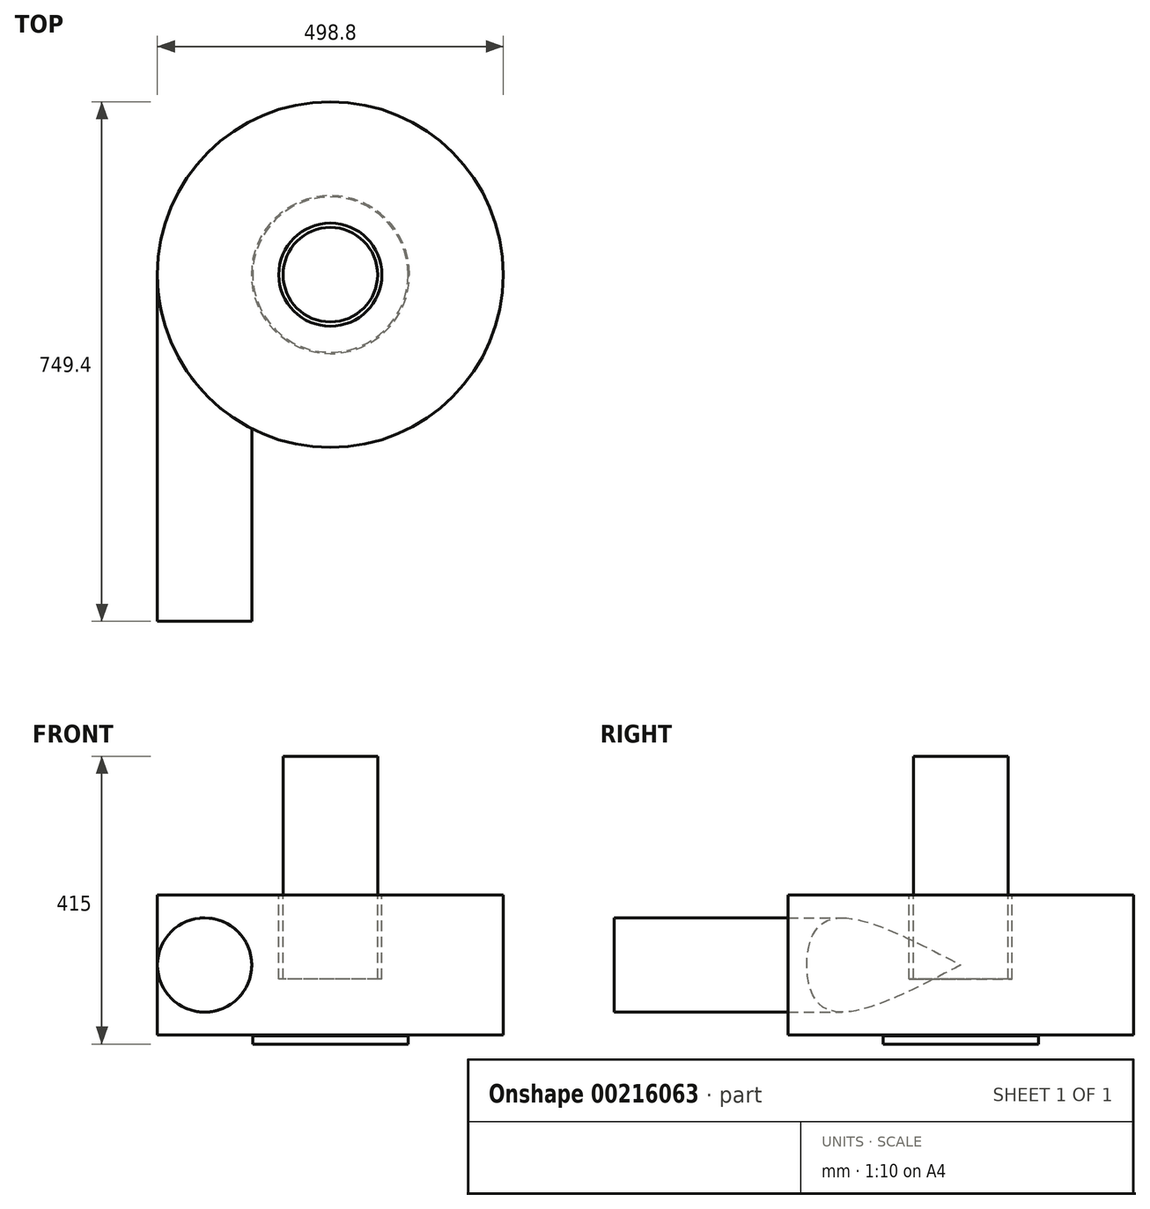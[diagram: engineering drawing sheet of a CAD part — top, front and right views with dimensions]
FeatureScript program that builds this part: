
annotation { "Feature Type Name" : "Feature", "Feature Type Description" : "" }
export const myFeature = defineFeature(function(context is Context, id is Id, definition is map)
    precondition{}
    {
        {
            var Q0;
            Q0=qCreatedBy(makeId("Front.planeOp"),FACE);
            var sketch = newSketch(context, id + "F0", { "sketchPlane" : qUnion([Q0])});
            skLineSegment(sketch, "E0", {"start": v(-114, 169) * mm, "end": v(-249.4, 169) * mm});
            skLineSegment(sketch, "E1", {"start": v(-249.4, 169) * mm, "end": v(-249.4, 371) * mm});
            skLineSegment(sketch, "E2", {"start": v(-249.4, 371) * mm, "end": v(-74.4, 371) * mm});
            skLineSegment(sketch, "E3", {"start": v(-74.4, 371) * mm, "end": v(-74.4, 250) * mm});
            skLineSegment(sketch, "E4", {"start": v(-74.4, 250) * mm, "end": v(-68.2, 250) * mm});
            skLineSegment(sketch, "E5", {"start": v(-68.2, 250) * mm, "end": v(-68.2, 371) * mm});
            skLineSegment(sketch, "E6", {"start": v(-68.2, 371) * mm, "end": v(0, 371) * mm});
            skLineSegment(sketch, "E7", {"start": v(-114, 169) * mm, "end": v(-112, 168) * mm});
            skLineSegment(sketch, "E8", {"start": v(-112, 168) * mm, "end": v(-112, 156) * mm});
            skLineSegment(sketch, "E9", {"start": v(-112, 156) * mm, "end": v(0, 156) * mm});
            skLineSegment(sketch, "E10", {"start": v(0, 371) * mm, "end": v(0, 156) * mm});
            skSolve(sketch);
        }
        {
            var Q0;
            Q0=makeQuery(id+"F0.imprint","IMPRINT",FACE,{"disambiguationData":[TD([[makeQuery(id+"F0.imprint","IMPRINT",EDGE,{"derivedFrom":sQuery(id+"F0.wireOp",EDGE,"E0")}),-1.0]])]});
            var Q1;
            Q1=sQuery(id+"F0.wireOp",EDGE,"E10");
            revolve(context, id + "F1", {"entities" : qUnion([Q0]), "axis" : qUnion([Q1]), "revolveType" : RevolveType.FULL});
        }
        {
            var Q0;
            Q0=qCreatedBy(makeId("Front.planeOp"),FACE);
            var sketch = newSketch(context, id + "F2", { "sketchPlane" : qUnion([Q0])});
            skCircle(sketch, "E11", {"center": v(-181.4, 270) * mm, "radius": 68 * mm});
            skSolve(sketch);
        }
        {
            var Q0;
            Q0=qSketchRegion(id+"F2",true);
            extrude(context, id + "F3", {"entities" : qUnion([Q0]), "operationType" : NewBodyOperationType.ADD, "depth" : 500 * mm});
        }
        {
            var Q0;
            Q0=makeQuery(id+"F1.opRevolve","SWEPT_FACE",FACE,{"disambiguationData":[OSD([sQuery(id+"F0.wireOp",EDGE,"E6")])]});
            extrude(context, id + "F4", {"entities" : qUnion([Q0]), "operationType" : NewBodyOperationType.ADD, "depth" : 200 * mm});
        }
    });
